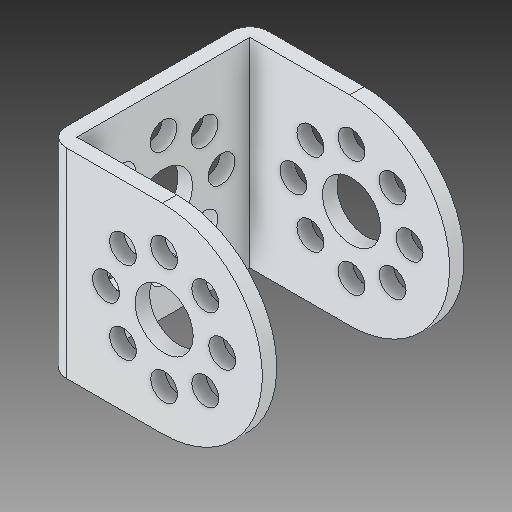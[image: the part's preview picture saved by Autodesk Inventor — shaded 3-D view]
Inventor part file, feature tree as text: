
AUTODESK INVENTOR PART (.ipt)
format: ipt  version: 2018 (Build 220112000, 112)  size: 226,816 bytes
history: native  units: in
note: dims shown in document units (in); Inventor stores cm internally (conversion verified against a paired STEP export)
features: fillet x1
ambient origin geometry x8: Origin, YZ Plane, XZ Plane, XY Plane, X Axis, Y Axis, Z Axis, Center Point
bodies: Solid1 (feature_tree)
feature tree (1):
  fillet  "Fillet2"  [1 undecoded]
note: 1 required parameter value undecoded (feature->parameter linkage not recoverable at this tier; creation-order binding heuristic only, values carry confidence <= 0.55)
